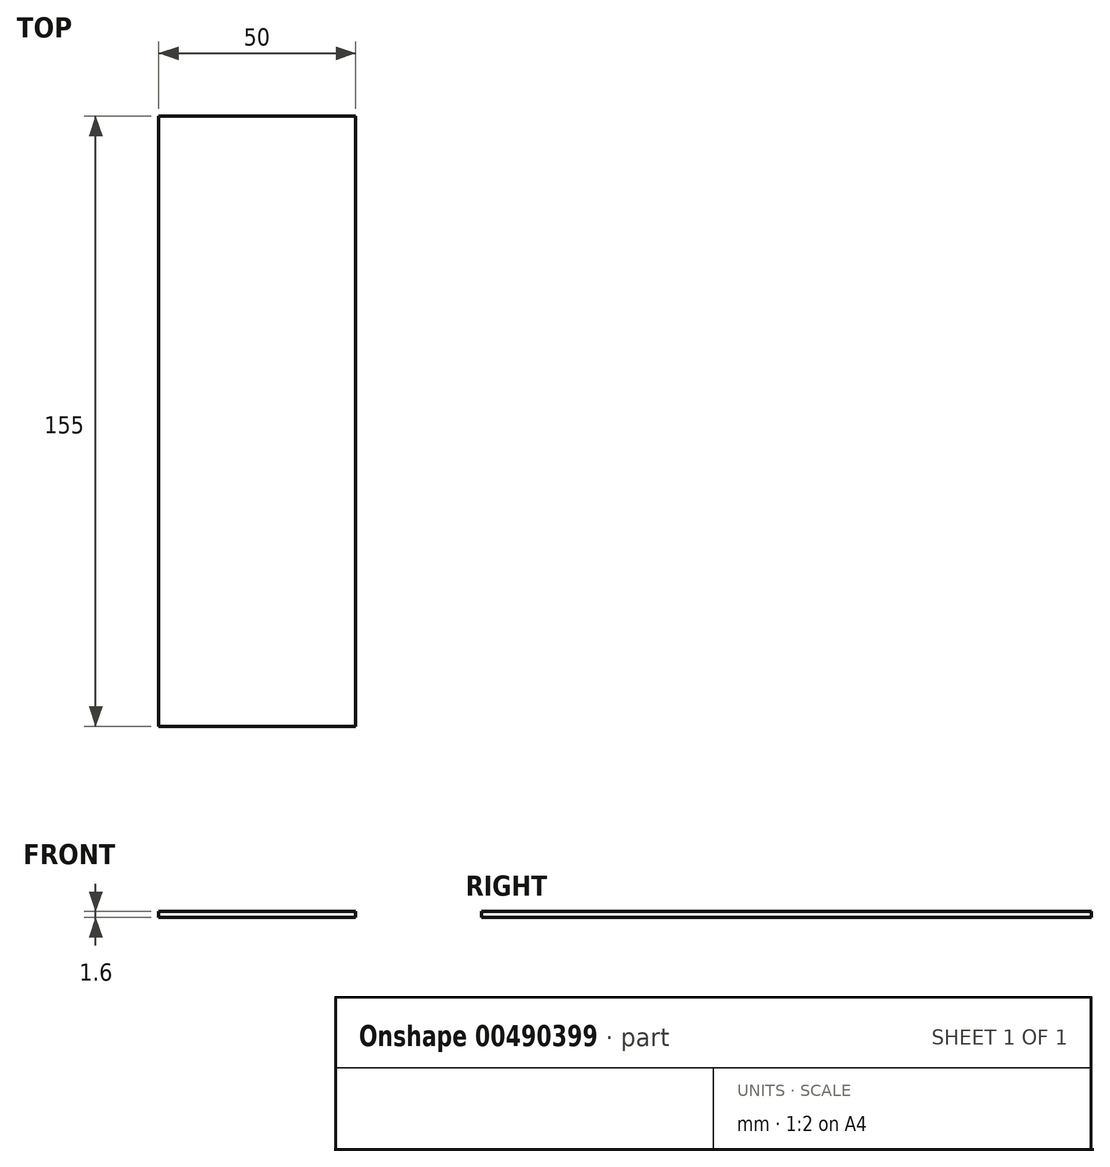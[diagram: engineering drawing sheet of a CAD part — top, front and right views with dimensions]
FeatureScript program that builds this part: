
annotation { "Feature Type Name" : "Feature", "Feature Type Description" : "" }
export const myFeature = defineFeature(function(context is Context, id is Id, definition is map)
    precondition{}
    {
        {
            var Q0;
            Q0=qCreatedBy(makeId("Top.planeOp"),FACE);
            var sketch = newSketch(context, id + "F0", { "sketchPlane" : qUnion([Q0])});
            skLineSegment(sketch, "E0.bottom", {"start": v(25, -77.5) * mm, "end": v(-25, -77.5) * mm});
            skLineSegment(sketch, "E0.top", {"start": v(25, 77.5) * mm, "end": v(-25, 77.5) * mm});
            skLineSegment(sketch, "E0.left", {"start": v(25, -77.5) * mm, "end": v(25, 77.5) * mm});
            skLineSegment(sketch, "E0.right", {"start": v(-25, -77.5) * mm, "end": v(-25, 77.5) * mm});
            skPoint(sketch, "E0.middle", {"position": v(0, 0) * mm});
            skSolve(sketch);
        }
        {
            var Q0;
            Q0=makeQuery(id+"F0.imprint","IMPRINT",FACE,{"disambiguationData":[TD([[makeQuery(id+"F0.imprint","IMPRINT",EDGE,{"derivedFrom":sQuery(id+"F0.wireOp",EDGE,"E0.bottom")}),-1.0]])]});
            extrude(context, id + "F1", {"entities" : qUnion([Q0]), "depth" : 1.6 * mm, "offsetDistance" : 25 * mm});
        }
    });
